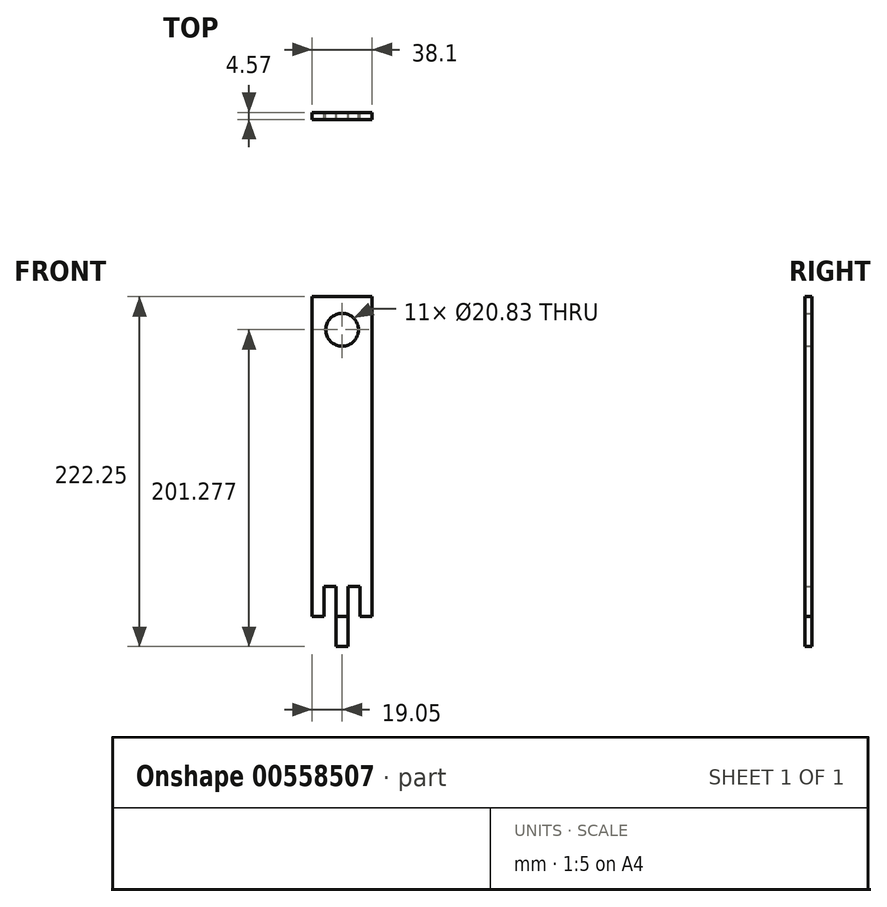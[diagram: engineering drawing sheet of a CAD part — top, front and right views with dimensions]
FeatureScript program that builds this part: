
annotation { "Feature Type Name" : "Feature", "Feature Type Description" : "" }
export const myFeature = defineFeature(function(context is Context, id is Id, definition is map)
    precondition{}
    {
        {
            var Q0;
            Q0=qCreatedBy(makeId("Front.planeOp"),FACE);
            var sketch = newSketch(context, id + "F0", { "sketchPlane" : qUnion([Q0])});
            skLineSegment(sketch, "E0.bottom", {"start": v(19.05, -101.6) * mm, "end": v(-19.05, -101.6) * mm});
            skLineSegment(sketch, "E0.top", {"start": v(19.05, 101.6) * mm, "end": v(-19.05, 101.6) * mm});
            skLineSegment(sketch, "E0.left", {"start": v(19.05, -101.6) * mm, "end": v(19.05, 101.6) * mm});
            skLineSegment(sketch, "E0.right", {"start": v(-19.05, -101.6) * mm, "end": v(-19.05, 101.6) * mm});
            skPoint(sketch, "E0.middle", {"position": v(0, 0) * mm});
            skCircle(sketch, "E1", {"center": v(0, 80.63) * mm, "radius": 10.41 * mm});
            skLineSegment(sketch, "E2.bottom", {"start": v(-3.8, -101.6) * mm, "end": v(-11.43, -101.6) * mm});
            skLineSegment(sketch, "E2.top", {"start": v(-3.8, -82.55) * mm, "end": v(-11.43, -82.55) * mm});
            skLineSegment(sketch, "E2.left", {"start": v(-3.8, -101.6) * mm, "end": v(-3.8, -82.55) * mm});
            skLineSegment(sketch, "E2.right", {"start": v(-11.43, -101.6) * mm, "end": v(-11.43, -82.55) * mm});
            skPoint(sketch, "E2.middle", {"position": v(-7.62, -92.08) * mm});
            skPoint(sketch, "E3.middle", {"position": v(-86.79, -40.9) * mm});
            skLineSegment(sketch, "E4.bottom", {"start": v(11.43, -82.55) * mm, "end": v(3.81, -82.55) * mm});
            skLineSegment(sketch, "E4.top", {"start": v(11.43, -101.6) * mm, "end": v(3.81, -101.6) * mm});
            skLineSegment(sketch, "E4.left", {"start": v(11.43, -82.55) * mm, "end": v(11.43, -101.6) * mm});
            skLineSegment(sketch, "E4.right", {"start": v(3.81, -82.55) * mm, "end": v(3.81, -101.6) * mm});
            skPoint(sketch, "E4.middle", {"position": v(7.62, -92.08) * mm});
            skLineSegment(sketch, "E5.bottom", {"start": v(3.8, -101.6) * mm, "end": v(-3.81, -101.6) * mm});
            skLineSegment(sketch, "E5.top", {"start": v(3.8, -120.65) * mm, "end": v(-3.81, -120.65) * mm});
            skLineSegment(sketch, "E5.left", {"start": v(3.81, -101.6) * mm, "end": v(3.81, -120.65) * mm});
            skLineSegment(sketch, "E5.right", {"start": v(-3.8, -101.6) * mm, "end": v(-3.8, -120.65) * mm});
            skPoint(sketch, "E5.middle", {"position": v(0, -111.13) * mm});
            skLineSegment(sketch, "E6.bottom", {"start": v(19.05, -101.6) * mm, "end": v(11.43, -101.6) * mm});
            skLineSegment(sketch, "E7.left", {"start": v(-19.05, -101.6) * mm, "end": v(-19.05, -101.6) * mm});
            skLineSegment(sketch, "E7.right", {"start": v(-11.43, -101.6) * mm, "end": v(-11.43, -101.6) * mm});
            skSolve(sketch);
        }
        {
            var Q0;
            Q0=makeQuery(id+"F0.imprint","IMPRINT",FACE,{"disambiguationData":[TD([[makeQuery(id+"F0.imprint","IMPRINT",EDGE,{"derivedFrom":sQuery(id+"F0.wireOp",EDGE,"E0.top")}),1.0]])]});
            var Q1;
            Q1=makeQuery(id+"F0.imprint","IMPRINT",FACE,{"disambiguationData":[TD([[makeQuery(id+"F0.imprint","IMPRINT",EDGE,{"derivedFrom":sQuery(id+"F0.wireOp",EDGE,"E5.bottom")}),1.0]])]});
            var Q2;
            {var subQ5=sQuery(id+"F0.wireOp",EDGE,"E5.top");Q2=makeQuery(id+"F0.imprint","IMPRINT",FACE,{"disambiguationData":[TD([[makeQuery(id+"F0.imprint","IMPRINT",EDGE,{"derivedFrom":subQ5}),-1.0]])]});}
            extrude(context, id + "F1", {"entities" : qUnion([Q0, Q1, Q2]), "depth" : 4.57 * mm, "offsetDistance" : 25.4 * mm});
        }
    });
